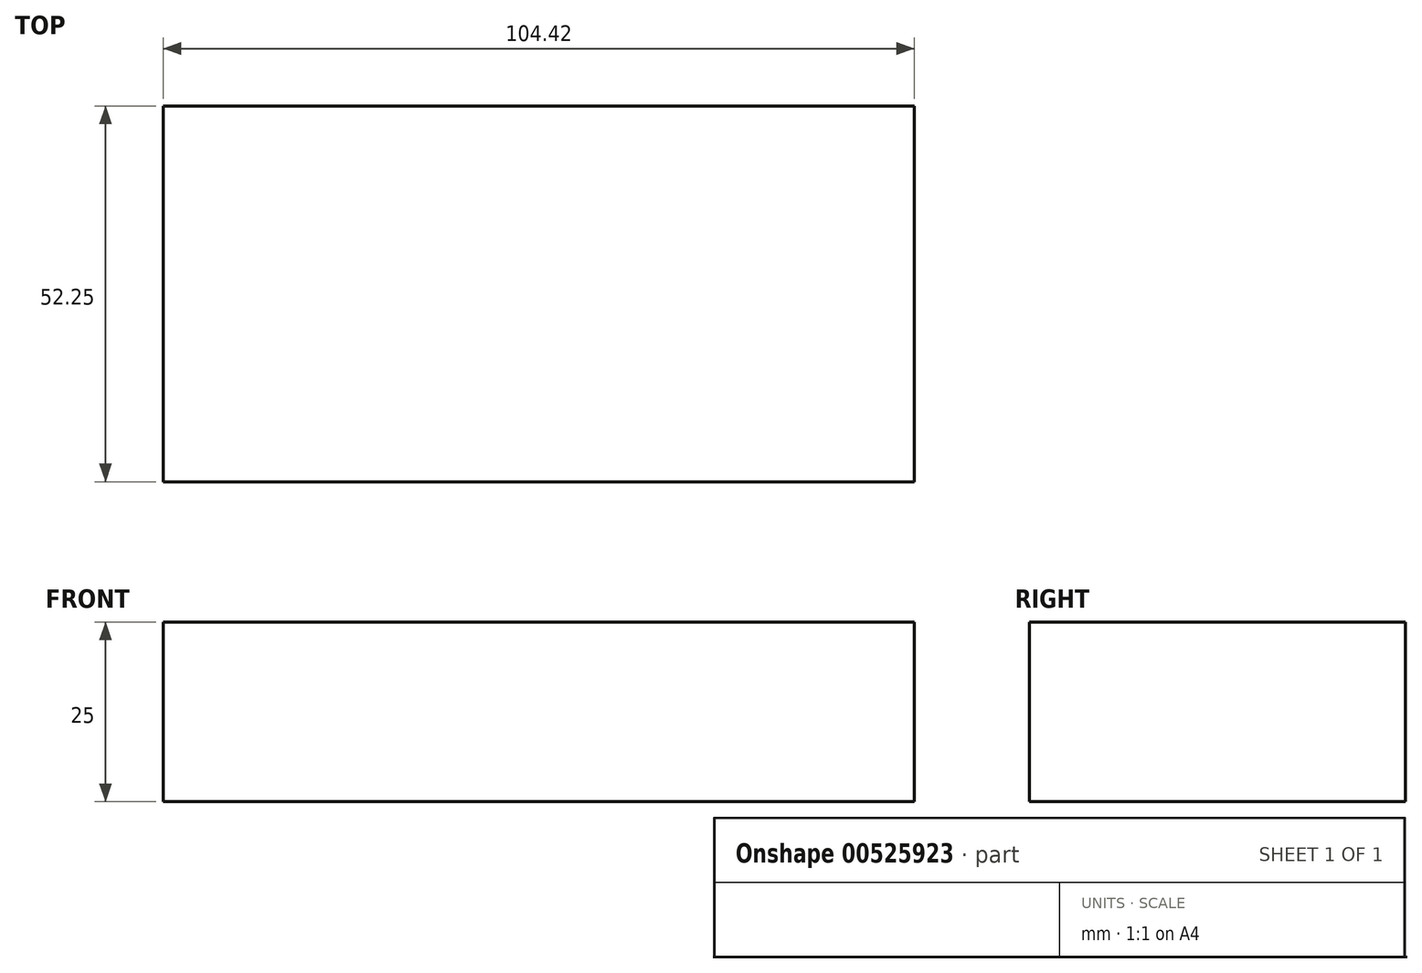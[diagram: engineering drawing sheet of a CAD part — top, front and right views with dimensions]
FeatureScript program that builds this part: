
annotation { "Feature Type Name" : "Feature", "Feature Type Description" : "" }
export const myFeature = defineFeature(function(context is Context, id is Id, definition is map)
    precondition{}
    {
        {
            var Q0;
            Q0=qCreatedBy(makeId("Top.planeOp"),FACE);
            var sketch = newSketch(context, id + "F0", { "sketchPlane" : qUnion([Q0])});
            skLineSegment(sketch, "E0.bottom", {"start": v(-38.41, 29.84) * mm, "end": v(66.01, 29.84) * mm});
            skLineSegment(sketch, "E0.top", {"start": v(-38.41, -22.4) * mm, "end": v(66.01, -22.4) * mm});
            skLineSegment(sketch, "E0.left", {"start": v(-38.41, 29.84) * mm, "end": v(-38.41, -22.4) * mm});
            skLineSegment(sketch, "E0.right", {"start": v(66.01, 29.84) * mm, "end": v(66.01, -22.4) * mm});
            skSolve(sketch);
        }
        {
            var Q0;
            Q0 = qSketchRegion(id + "F0", true);
            extrude(context, id + "F1", {"entities" : qUnion([Q0]), "oppositeDirection" : true, "depth" : 25 * mm, "offsetDistance" : 25 * mm});
        }
    });
